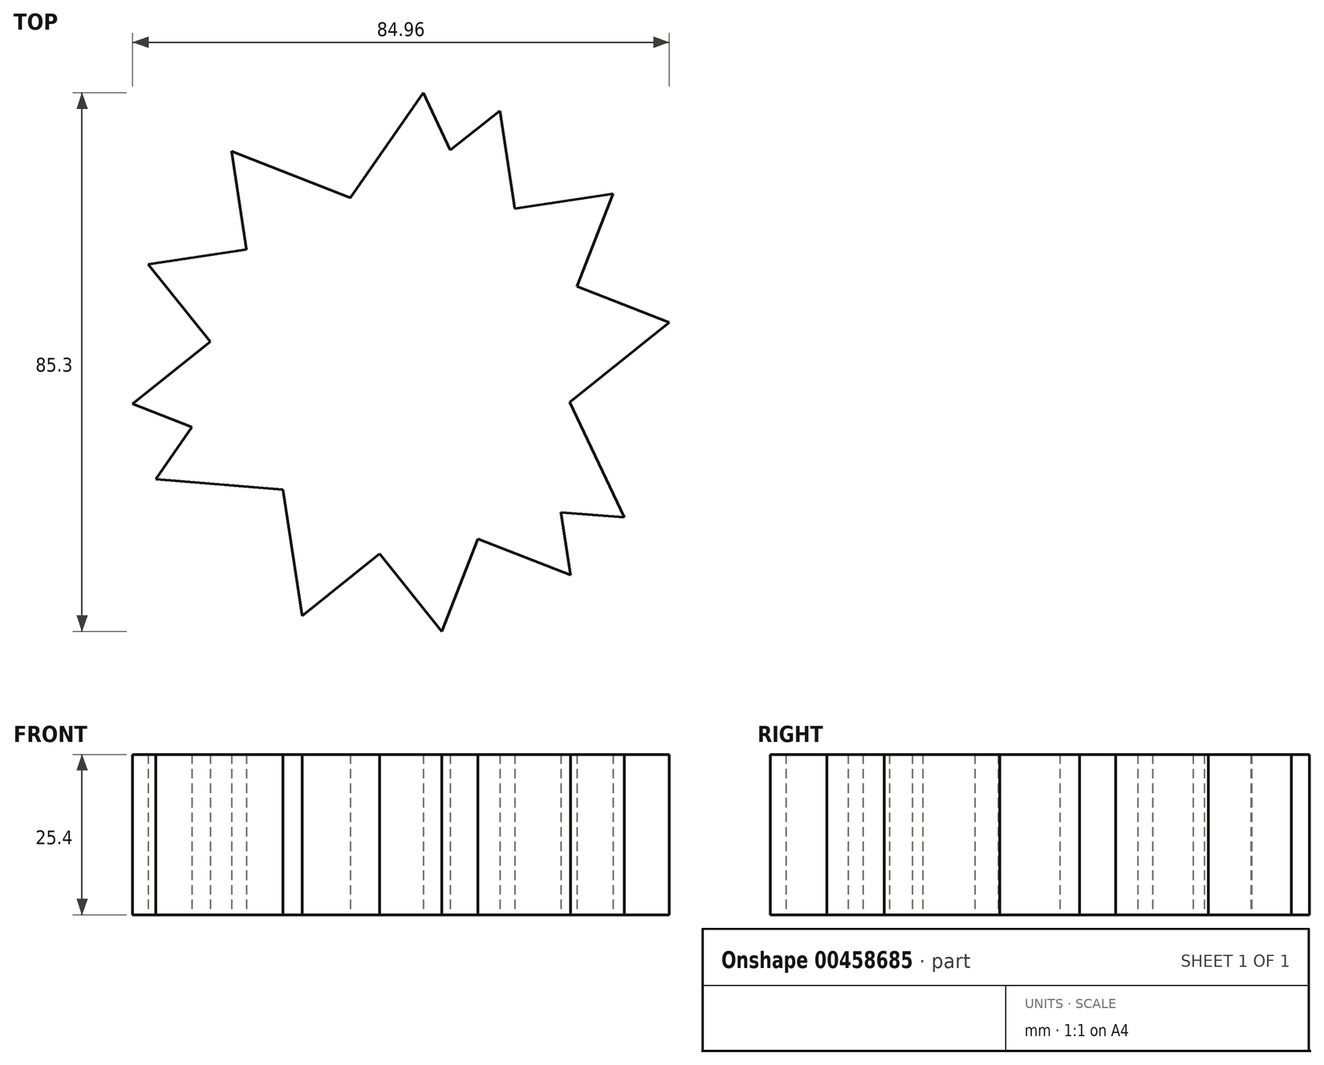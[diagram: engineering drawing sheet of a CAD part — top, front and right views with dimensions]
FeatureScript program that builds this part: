
annotation { "Feature Type Name" : "Feature", "Feature Type Description" : "" }
export const myFeature = defineFeature(function(context is Context, id is Id, definition is map)
    precondition{}
    {
        {
            var Q0;
            Q0=qCreatedBy(makeId("Top.planeOp"),FACE);
            var sketch = newSketch(context, id + "F0", { "sketchPlane" : qUnion([Q0])});
            skCircle(sketch, "E0.cCircle", {"center": v(0, 0) * mm, "radius": 21.48 * mm, "construction": true});
            skLineSegment(sketch, "E0.0", {"start": v(33.57, 26.81) * mm, "end": v(6.44, -42.48) * mm});
            skLineSegment(sketch, "E0.1", {"start": v(6.44, -42.48) * mm, "end": v(-40, 15.67) * mm});
            skLineSegment(sketch, "E0.2", {"start": v(-40, 15.67) * mm, "end": v(33.57, 26.81) * mm});
            skPoint(sketch, "E0.0.midPoint", {"position": v(20, -7.83) * mm});
            skLineSegment(sketch, "E1.0", {"start": v(-38.83, -18.38) * mm, "end": v(3.5, 42.82) * mm});
            skLineSegment(sketch, "E1.1", {"start": v(3.5, 42.82) * mm, "end": v(35.33, -24.44) * mm});
            skLineSegment(sketch, "E1.2", {"start": v(35.33, -24.44) * mm, "end": v(-38.83, -18.38) * mm});
            skPoint(sketch, "E1.0.midPoint", {"position": v(-17.67, 12.22) * mm});
            skLineSegment(sketch, "E2.0", {"start": v(-15.67, -40) * mm, "end": v(-26.81, 33.57) * mm});
            skLineSegment(sketch, "E2.1", {"start": v(-26.81, 33.57) * mm, "end": v(42.48, 6.44) * mm});
            skLineSegment(sketch, "E2.2", {"start": v(42.48, 6.44) * mm, "end": v(-15.67, -40) * mm});
            skPoint(sketch, "E2.0.midPoint", {"position": v(-21.24, -3.22) * mm});
            skLineSegment(sketch, "E3.0", {"start": v(15.67, 40) * mm, "end": v(26.81, -33.57) * mm});
            skLineSegment(sketch, "E3.1", {"start": v(26.81, -33.57) * mm, "end": v(-42.48, -6.44) * mm});
            skLineSegment(sketch, "E3.2", {"start": v(-42.48, -6.44) * mm, "end": v(15.67, 40) * mm});
            skPoint(sketch, "E3.0.midPoint", {"position": v(21.24, 3.22) * mm});
            skSolve(sketch);
        }
        {
            var Q0;
            Q0 = qSketchRegion(id + "F0", true);
            var Q1;
            {var subQ0=sQuery(id+"F0.wireOp",EDGE,"E3.0");var subQ1=sQuery(id+"F0.wireOp",EDGE,"E0.0");var subQ2=makeQuery(id+"F0.imprint","INTERSECT",VERTEX,{"derivedFrom":[subQ1,subQ0]});Q1=makeQuery(id+"F0.imprint","IMPRINT",FACE,{"disambiguationData":[TD([[makeQuery(id+"F0.imprint","IMPRINT",EDGE,{"disambiguationData":[TD([[subQ2,-1.0]])],"derivedFrom":subQ1}),-1.0]])]});}
            var Q2;
            {var subQ0=sQuery(id+"F0.wireOp",EDGE,"E2.1");var subQ1=sQuery(id+"F0.wireOp",EDGE,"E0.2");var subQ2=makeQuery(id+"F0.imprint","INTERSECT",VERTEX,{"derivedFrom":[subQ1,subQ0]});Q2=makeQuery(id+"F0.imprint","IMPRINT",FACE,{"disambiguationData":[TD([[makeQuery(id+"F0.imprint","IMPRINT",EDGE,{"disambiguationData":[TD([[subQ2,-1.0]])],"derivedFrom":subQ1}),-1.0]])]});}
            var Q3;
            {var subQ0=sQuery(id+"F0.wireOp",EDGE,"E2.1");var subQ1=sQuery(id+"F0.wireOp",EDGE,"E1.1");var subQ2=makeQuery(id+"F0.imprint","INTERSECT",VERTEX,{"derivedFrom":[subQ1,subQ0]});Q3=makeQuery(id+"F0.imprint","IMPRINT",FACE,{"disambiguationData":[TD([[makeQuery(id+"F0.imprint","IMPRINT",EDGE,{"disambiguationData":[TD([[subQ2,-1.0]])],"derivedFrom":subQ1}),1.0]])]});}
            var Q4;
            {var subQ0=sQuery(id+"F0.wireOp",EDGE,"E1.1");var subQ1=sQuery(id+"F0.wireOp",EDGE,"E0.0");var subQ2=makeQuery(id+"F0.imprint","INTERSECT",VERTEX,{"derivedFrom":[subQ1,subQ0]});Q4=makeQuery(id+"F0.imprint","IMPRINT",FACE,{"disambiguationData":[TD([[makeQuery(id+"F0.imprint","IMPRINT",EDGE,{"disambiguationData":[TD([[subQ2,-1.0]])],"derivedFrom":subQ1}),-1.0]])]});}
            var Q5;
            {var subQ0=sQuery(id+"F0.wireOp",EDGE,"E3.0");var subQ1=sQuery(id+"F0.wireOp",EDGE,"E0.0");var subQ2=makeQuery(id+"F0.imprint","INTERSECT",VERTEX,{"derivedFrom":[subQ1,subQ0]});Q5=makeQuery(id+"F0.imprint","IMPRINT",FACE,{"disambiguationData":[TD([[makeQuery(id+"F0.imprint","IMPRINT",EDGE,{"disambiguationData":[TD([[subQ2,-1.0]])],"derivedFrom":subQ1}),1.0]])]});}
            var Q6;
            {var subQ0=sQuery(id+"F0.wireOp",EDGE,"E2.2");var subQ1=sQuery(id+"F0.wireOp",EDGE,"E0.0");var subQ2=makeQuery(id+"F0.imprint","INTERSECT",VERTEX,{"derivedFrom":[subQ1,subQ0]});Q6=makeQuery(id+"F0.imprint","IMPRINT",FACE,{"disambiguationData":[TD([[makeQuery(id+"F0.imprint","IMPRINT",EDGE,{"disambiguationData":[TD([[subQ2,-1.0]])],"derivedFrom":subQ1}),-1.0]])]});}
            var Q7;
            {var subQ0=sQuery(id+"F0.wireOp",EDGE,"E2.2");var subQ1=sQuery(id+"F0.wireOp",EDGE,"E1.2");var subQ2=makeQuery(id+"F0.imprint","INTERSECT",VERTEX,{"derivedFrom":[subQ1,subQ0]});Q7=makeQuery(id+"F0.imprint","IMPRINT",FACE,{"disambiguationData":[TD([[makeQuery(id+"F0.imprint","IMPRINT",EDGE,{"disambiguationData":[TD([[subQ2,-1.0]])],"derivedFrom":subQ1}),1.0]])]});}
            var Q8;
            {var subQ0=sQuery(id+"F0.wireOp",EDGE,"E1.2");var subQ1=sQuery(id+"F0.wireOp",EDGE,"E0.1");var subQ2=makeQuery(id+"F0.imprint","INTERSECT",VERTEX,{"derivedFrom":[subQ1,subQ0]});Q8=makeQuery(id+"F0.imprint","IMPRINT",FACE,{"disambiguationData":[TD([[makeQuery(id+"F0.imprint","IMPRINT",EDGE,{"disambiguationData":[TD([[subQ2,-1.0]])],"derivedFrom":subQ1}),-1.0]])]});}
            var Q9;
            {var subQ0=sQuery(id+"F0.wireOp",EDGE,"E3.1");var subQ1=sQuery(id+"F0.wireOp",EDGE,"E0.1");var subQ2=makeQuery(id+"F0.imprint","INTERSECT",VERTEX,{"derivedFrom":[subQ1,subQ0]});Q9=makeQuery(id+"F0.imprint","IMPRINT",FACE,{"disambiguationData":[TD([[makeQuery(id+"F0.imprint","IMPRINT",EDGE,{"disambiguationData":[TD([[subQ2,-1.0]])],"derivedFrom":subQ1}),1.0]])]});}
            var Q10;
            {var subQ0=sQuery(id+"F0.wireOp",EDGE,"E2.0");var subQ1=sQuery(id+"F0.wireOp",EDGE,"E0.1");var subQ2=makeQuery(id+"F0.imprint","INTERSECT",VERTEX,{"derivedFrom":[subQ1,subQ0]});Q10=makeQuery(id+"F0.imprint","IMPRINT",FACE,{"disambiguationData":[TD([[makeQuery(id+"F0.imprint","IMPRINT",EDGE,{"disambiguationData":[TD([[subQ2,-1.0]])],"derivedFrom":subQ1}),-1.0]])]});}
            var Q11;
            {var subQ0=sQuery(id+"F0.wireOp",EDGE,"E2.0");var subQ1=sQuery(id+"F0.wireOp",EDGE,"E1.0");var subQ2=makeQuery(id+"F0.imprint","INTERSECT",VERTEX,{"derivedFrom":[subQ1,subQ0]});Q11=makeQuery(id+"F0.imprint","IMPRINT",FACE,{"disambiguationData":[TD([[makeQuery(id+"F0.imprint","IMPRINT",EDGE,{"disambiguationData":[TD([[subQ2,-1.0]])],"derivedFrom":subQ1}),1.0]])]});}
            var Q12;
            {var subQ0=sQuery(id+"F0.wireOp",EDGE,"E1.0");var subQ1=sQuery(id+"F0.wireOp",EDGE,"E0.2");var subQ2=makeQuery(id+"F0.imprint","INTERSECT",VERTEX,{"derivedFrom":[subQ1,subQ0]});Q12=makeQuery(id+"F0.imprint","IMPRINT",FACE,{"disambiguationData":[TD([[makeQuery(id+"F0.imprint","IMPRINT",EDGE,{"disambiguationData":[TD([[subQ2,-1.0]])],"derivedFrom":subQ1}),-1.0]])]});}
            var Q13;
            {var subQ0=sQuery(id+"F0.wireOp",EDGE,"E3.2");var subQ1=sQuery(id+"F0.wireOp",EDGE,"E0.2");var subQ2=makeQuery(id+"F0.imprint","INTERSECT",VERTEX,{"derivedFrom":[subQ1,subQ0]});Q13=makeQuery(id+"F0.imprint","IMPRINT",FACE,{"disambiguationData":[TD([[makeQuery(id+"F0.imprint","IMPRINT",EDGE,{"disambiguationData":[TD([[subQ2,-1.0]])],"derivedFrom":subQ1}),1.0]])]});}
            extrude(context, id + "F1", {"entities" : qUnion([Q0, Q1, Q2, Q3, Q4, Q5, Q6, Q7, Q8, Q9, Q10, Q11, Q12, Q13]), "depth" : 25.4 * mm});
        }
    });
